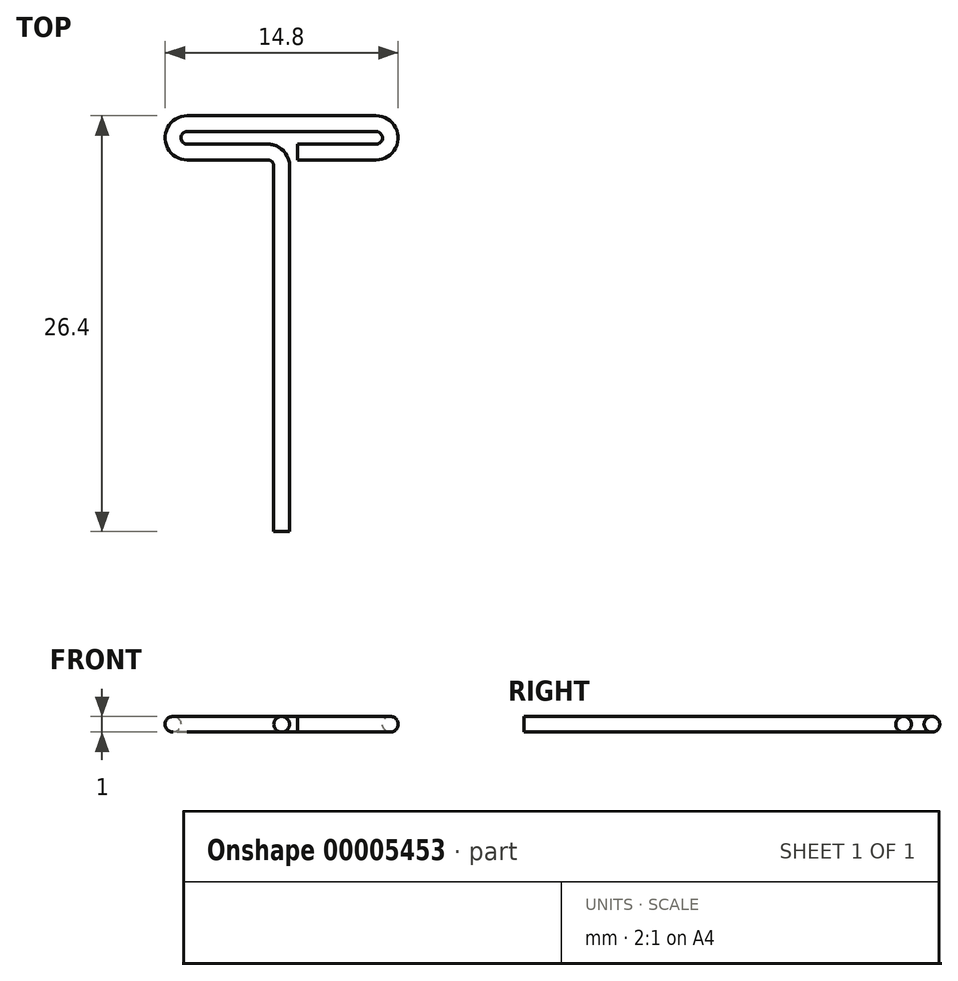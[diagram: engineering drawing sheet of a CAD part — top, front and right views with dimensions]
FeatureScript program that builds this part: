
annotation { "Feature Type Name" : "Feature", "Feature Type Description" : "" }
export const myFeature = defineFeature(function(context is Context, id is Id, definition is map)
    precondition{}
    {
        {
            var Q0;
            Q0=qCreatedBy(makeId("Top.planeOp"),FACE);
            var sketch = newSketch(context, id + "F0", { "sketchPlane" : qUnion([Q0])});
            skLineSegment(sketch, "E0", {"start": v(0, 0) * mm, "end": v(0, 23.2) * mm});
            skArc(sketch, "E1", {"start": v(0, 23.2) * mm, "mid": v(-0.26, 23.84) * mm, "end": v(-0.9, 24.1) * mm});
            skLineSegment(sketch, "E2", {"start": v(-0.9, 24.1) * mm, "end": v(-6, 24.1) * mm});
            skArc(sketch, "E3", {"start": v(-6, 24.1) * mm, "mid": v(-6.9, 25) * mm, "end": v(-6, 25.9) * mm});
            skLineSegment(sketch, "E4", {"start": v(-6, 25.9) * mm, "end": v(6, 25.9) * mm});
            skArc(sketch, "E5", {"start": v(6, 25.9) * mm, "mid": v(6.9, 25) * mm, "end": v(6, 24.1) * mm});
            skLineSegment(sketch, "E6", {"start": v(6, 24.1) * mm, "end": v(1, 24.1) * mm});
            skLineSegment(sketch, "E7", {"start": v(-6, 25) * mm, "end": v(6, 25) * mm, "construction": true});
            skLineSegment(sketch, "E8", {"start": v(0, 23.2) * mm, "end": v(0, 25) * mm, "construction": true});
            skSolve(sketch);
        }
        {
            var Q0;
            Q0=qCreatedBy(makeId("Front.planeOp"),FACE);
            var sketch = newSketch(context, id + "F1", { "sketchPlane" : qUnion([Q0])});
            skCircle(sketch, "E9", {"center": v(0, 0) * mm, "radius": 0.5 * mm});
            skSolve(sketch);
        }
        {
            var Q0;
            Q0=makeQuery(id+"F1.imprint","IMPRINT",FACE,{"disambiguationData":[TD([[makeQuery(id+"F1.imprint","IMPRINT",EDGE,{"derivedFrom":sQuery(id+"F1.wireOp",EDGE,"E9")}),1.0]])]});
            var Q1;
            Q1=sQuery(id+"F0.wireOp",EDGE,"E0");
            var Q2;
            Q2=sQuery(id+"F0.wireOp",EDGE,"E1");
            var Q3;
            Q3=sQuery(id+"F0.wireOp",EDGE,"E2");
            var Q4;
            Q4=sQuery(id+"F0.wireOp",EDGE,"E3");
            var Q5;
            Q5=sQuery(id+"F0.wireOp",EDGE,"E4");
            var Q6;
            Q6=sQuery(id+"F0.wireOp",EDGE,"E5");
            var Q7;
            Q7=sQuery(id+"F0.wireOp",EDGE,"E6");
            sweep(context, id + "F2", {"profiles" : qUnion([Q0]), "path" : qUnion([Q1, Q2, Q3, Q4, Q5, Q6, Q7])});
        }
    });
